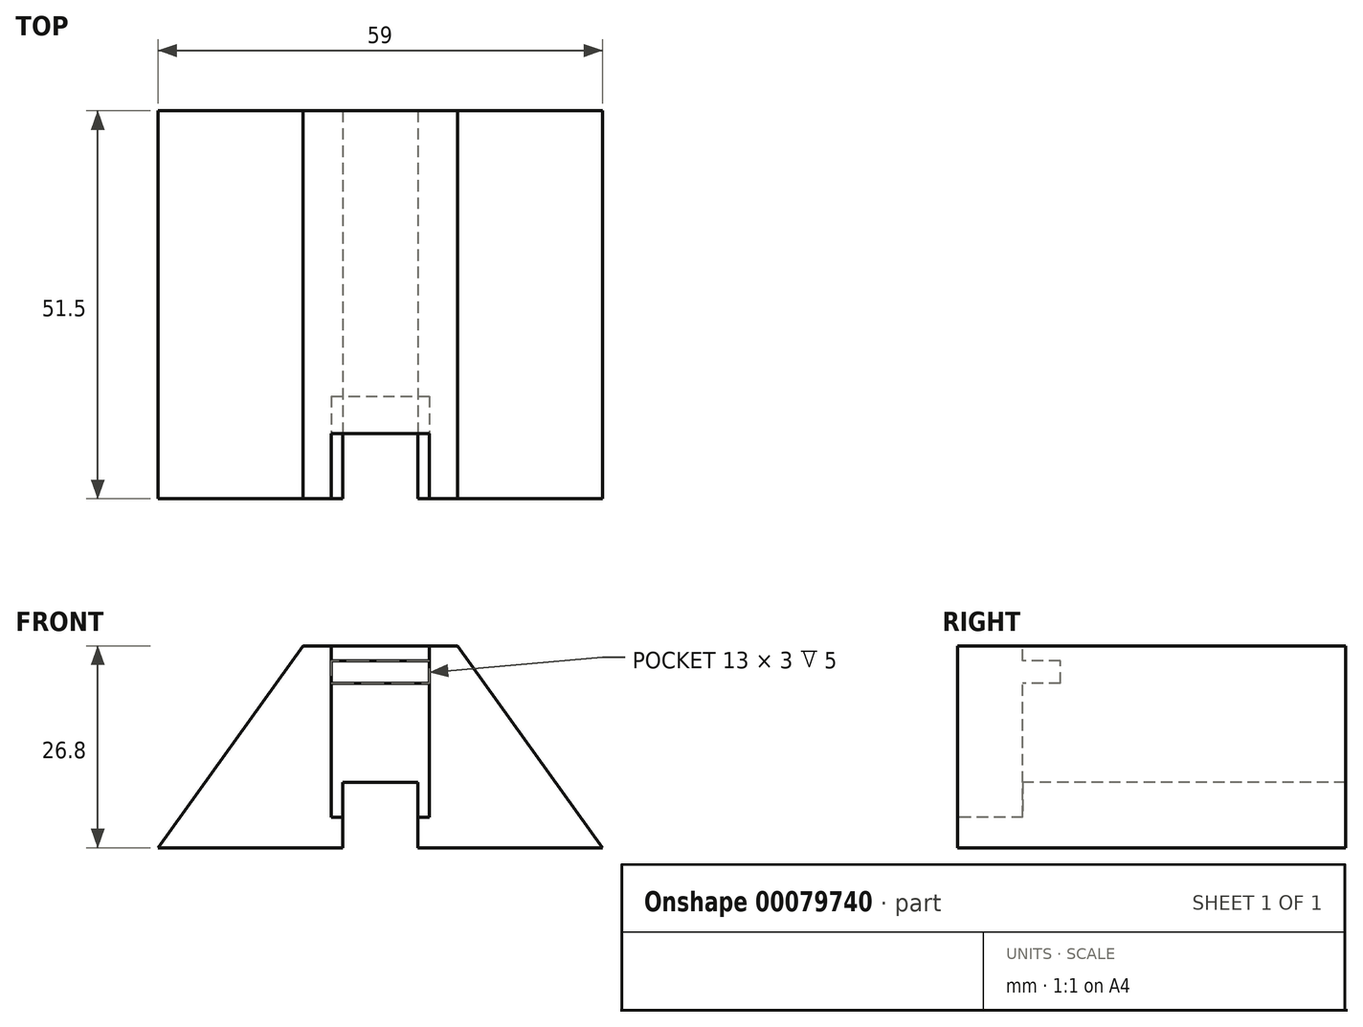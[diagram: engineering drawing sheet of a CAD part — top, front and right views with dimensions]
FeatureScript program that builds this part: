
annotation { "Feature Type Name" : "Feature", "Feature Type Description" : "" }
export const myFeature = defineFeature(function(context is Context, id is Id, definition is map)
    precondition{}
    {
        {
            var Q0;
            Q0=qCreatedBy(makeId("Top.planeOp"),FACE);
            var sketch = newSketch(context, id + "F0", { "sketchPlane" : qUnion([Q0])});
            skLineSegment(sketch, "E0.bottom", {"start": v(-29.5, 25.75) * mm, "end": v(29.5, 25.75) * mm});
            skLineSegment(sketch, "E0.top", {"start": v(-29.5, -25.75) * mm, "end": v(29.5, -25.75) * mm});
            skLineSegment(sketch, "E0.left", {"start": v(-29.5, 25.75) * mm, "end": v(-29.5, -25.75) * mm});
            skLineSegment(sketch, "E0.right", {"start": v(29.5, 25.75) * mm, "end": v(29.5, -25.75) * mm});
            skPoint(sketch, "E0.middle", {"position": v(0, 0) * mm});
            skSolve(sketch);
        }
        {
            var Q0;
            Q0=makeQuery(id+"F0.imprint","IMPRINT",FACE,{"disambiguationData":[TD([[makeQuery(id+"F0.imprint","IMPRINT",EDGE,{"derivedFrom":sQuery(id+"F0.wireOp",EDGE,"E0.bottom")}),-1.0]])]});
            extrude(context, id + "F1", {"entities" : qUnion([Q0]), "depth" : 26.8 * mm});
        }
        {
            var Q0;
            Q0=makeQuery(id+"F1.opExtrude","CAP_FACE",FACE,{"disambiguationData":[OSD([sQuery(id+"F0.wireOp",EDGE,"E0.bottom"),sQuery(id+"F0.wireOp",EDGE,"E0.top"),sQuery(id+"F0.wireOp",EDGE,"E0.left"),sQuery(id+"F0.wireOp",EDGE,"E0.right")])],"isStart":false});
            var sketch = newSketch(context, id + "F2", { "sketchPlane" : qUnion([Q0])});
            skLineSegment(sketch, "E1.bottom", {"start": v(-5, -17.1) * mm, "end": v(5, -17.1) * mm});
            skLineSegment(sketch, "E1.top", {"start": v(-5, -25.75) * mm, "end": v(5, -25.75) * mm});
            skLineSegment(sketch, "E1.left", {"start": v(-5, -17.1) * mm, "end": v(-5, -25.75) * mm});
            skLineSegment(sketch, "E1.right", {"start": v(5, -17.1) * mm, "end": v(5, -25.75) * mm});
            skPoint(sketch, "E1.middle", {"position": v(0, -21.43) * mm});
            skSolve(sketch);
        }
        {
            var Q0;
            Q0=makeQuery(id+"F2.imprint","IMPRINT",FACE,{"disambiguationData":[TD([[makeQuery(id+"F2.imprint","IMPRINT",EDGE,{"derivedFrom":sQuery(id+"F2.wireOp",EDGE,"E1.bottom")}),-1.0]])]});
            extrude(context, id + "F3", {"entities" : qUnion([Q0]), "operationType" : NewBodyOperationType.REMOVE, "oppositeDirection" : true, "depth" : 26.8 * mm});
        }
        {
            var Q0;
            Q0=makeQuery(id+"F1.opExtrude","CAP_FACE",FACE,{"disambiguationData":[OSD([sQuery(id+"F0.wireOp",EDGE,"E0.bottom"),sQuery(id+"F0.wireOp",EDGE,"E0.top"),sQuery(id+"F0.wireOp",EDGE,"E0.left"),sQuery(id+"F0.wireOp",EDGE,"E0.right")])],"isStart":false});
            var sketch = newSketch(context, id + "F4", { "sketchPlane" : qUnion([Q0])});
            skLineSegment(sketch, "E2.bottom", {"start": v(-6.5, -17.1) * mm, "end": v(6.5, -17.1) * mm});
            skLineSegment(sketch, "E2.top", {"start": v(-6.5, -25.75) * mm, "end": v(6.5, -25.75) * mm});
            skLineSegment(sketch, "E2.left", {"start": v(-6.5, -17.1) * mm, "end": v(-6.5, -25.75) * mm});
            skLineSegment(sketch, "E2.right", {"start": v(6.5, -17.1) * mm, "end": v(6.5, -25.75) * mm});
            skPoint(sketch, "E2.middle", {"position": v(0, -21.43) * mm});
            skSolve(sketch);
        }
        {
            var Q0;
            {var subQ3=sQuery(id+"F4.wireOp",EDGE,"E2.left");Q0=makeQuery(id+"F4.imprint","IMPRINT",FACE,{"disambiguationData":[TD([[makeQuery(id+"F4.imprint","IMPRINT",EDGE,{"derivedFrom":subQ3}),1.0]])]});}
            var Q1;
            {var subQ3=sQuery(id+"F4.wireOp",EDGE,"E2.right");Q1=makeQuery(id+"F4.imprint","IMPRINT",FACE,{"disambiguationData":[TD([[makeQuery(id+"F4.imprint","IMPRINT",EDGE,{"derivedFrom":subQ3}),-1.0]])]});}
            extrude(context, id + "F5", {"entities" : qUnion([Q0, Q1]), "operationType" : NewBodyOperationType.REMOVE, "oppositeDirection" : true, "depth" : 22.75 * mm});
        }
        {
            var Q0;
            {var subQ1=sQuery(id+"F0.wireOp",EDGE,"E0.left");var subQ2=sQuery(id+"F0.wireOp",EDGE,"E0.top");Q0=makeQuery(id+"F3.boolean.opBoolean","SPLIT",FACE,{"disambiguationData":[TD([makeQuery(id+"F1.opExtrude","SWEPT_FACE",FACE,{"disambiguationData":[OSD([subQ1])]})])],"derivedFrom":makeQuery(id+"F1.opExtrude","SWEPT_FACE",FACE,{"disambiguationData":[OSD([subQ2])]})});}
            var sketch = newSketch(context, id + "F6", { "sketchPlane" : qUnion([Q0])});
            skLineSegment(sketch, "E3", {"start": v(-29.5, 0) * mm, "end": v(-10.24, 26.8) * mm});
            skSolve(sketch);
        }
        {
            var Q0;
            {var subQ0=sQuery(id+"F6.wireOp",EDGE,"E3");Q0=makeQuery(id+"F6.imprint","IMPRINT",FACE,{"disambiguationData":[TD([[makeQuery(id+"F6.imprint","IMPRINT",EDGE,{"derivedFrom":subQ0}),1.0]])]});}
            extrude(context, id + "F7", {"entities" : qUnion([Q0]), "operationType" : NewBodyOperationType.REMOVE, "oppositeDirection" : true, "depth" : 51.5 * mm});
        }
        {
            var Q0;
            {var subQ0=sQuery(id+"F0.wireOp",EDGE,"E0.right");var subQ2=sQuery(id+"F0.wireOp",EDGE,"E0.top");Q0=makeQuery(id+"F3.boolean.opBoolean","SPLIT",FACE,{"disambiguationData":[TD([makeQuery(id+"F1.opExtrude","SWEPT_FACE",FACE,{"disambiguationData":[OSD([subQ0])]})])],"derivedFrom":makeQuery(id+"F1.opExtrude","SWEPT_FACE",FACE,{"disambiguationData":[OSD([subQ2])]})});}
            var sketch = newSketch(context, id + "F8", { "sketchPlane" : qUnion([Q0])});
            skLineSegment(sketch, "E4", {"start": v(29.5, 0) * mm, "end": v(10.24, 26.8) * mm});
            skSolve(sketch);
        }
        {
            var Q0;
            {var subQ0=sQuery(id+"F8.wireOp",EDGE,"E4");Q0=makeQuery(id+"F8.imprint","IMPRINT",FACE,{"disambiguationData":[TD([[makeQuery(id+"F8.imprint","IMPRINT",EDGE,{"derivedFrom":subQ0}),-1.0]])]});}
            extrude(context, id + "F9", {"entities" : qUnion([Q0]), "operationType" : NewBodyOperationType.REMOVE, "oppositeDirection" : true, "depth" : 51.5 * mm});
        }
        {
            var Q0;
            {var subQ0=sQuery(id+"F4.wireOp",EDGE,"E2.bottom");Q0=makeQuery(id+"F5.boolean.opBoolean","MERGE",FACE,{"derivedFrom":[makeQuery(id+"F3.boolean.opBoolean","COPY",FACE,{"derivedFrom":makeQuery(id+"F3.opExtrude","SWEPT_FACE",FACE,{"disambiguationData":[OSD([sQuery(id+"F2.wireOp",EDGE,"E1.bottom")])]})}),makeQuery(id+"F5.opExtrude","SWEPT_FACE",FACE,{"disambiguationData":[OSD([subQ0]),TDD([makeQuery(id+"F4.imprint","IMPRINT",EDGE,{"disambiguationData":[TD([[makeQuery(id+"F4.imprint","INTERSECT",VERTEX,{"derivedFrom":[makeQuery(id+"F3.boolean.opBoolean","COPY",EDGE,{"derivedFrom":makeQuery(id+"F3.opExtrude","CAP_EDGE",EDGE,{"disambiguationData":[OSD([sQuery(id+"F2.wireOp",EDGE,"E1.left")])],"isStart":true})}),subQ0]}),1.0]])],"derivedFrom":subQ0})])]}),makeQuery(id+"F5.opExtrude","SWEPT_FACE",FACE,{"disambiguationData":[OSD([subQ0]),TDD([makeQuery(id+"F4.imprint","IMPRINT",EDGE,{"disambiguationData":[TD([[makeQuery(id+"F4.imprint","INTERSECT",VERTEX,{"derivedFrom":[makeQuery(id+"F3.boolean.opBoolean","COPY",EDGE,{"derivedFrom":makeQuery(id+"F3.opExtrude","CAP_EDGE",EDGE,{"disambiguationData":[OSD([sQuery(id+"F2.wireOp",EDGE,"E1.right")])],"isStart":true})}),subQ0]}),-1.0]])],"derivedFrom":subQ0})])]})]});}
            var sketch = newSketch(context, id + "F10", { "sketchPlane" : qUnion([Q0])});
            skLineSegment(sketch, "E5.bottom", {"start": v(-5, 8.67) * mm, "end": v(5, 8.67) * mm});
            skLineSegment(sketch, "E5.top", {"start": v(-5, 0) * mm, "end": v(5, 0) * mm});
            skLineSegment(sketch, "E5.left", {"start": v(-5, 8.67) * mm, "end": v(-5, 0) * mm});
            skLineSegment(sketch, "E5.right", {"start": v(5, 8.67) * mm, "end": v(5, 0) * mm});
            skPoint(sketch, "E5.middle", {"position": v(0, 4.33) * mm});
            skSolve(sketch);
        }
        {
            var Q0;
            {var subQ4=sQuery(id+"F10.wireOp",EDGE,"E5.bottom");Q0=makeQuery(id+"F10.imprint","IMPRINT",FACE,{"disambiguationData":[TD([[makeQuery(id+"F10.imprint","IMPRINT",EDGE,{"derivedFrom":subQ4}),-1.0]])]});}
            extrude(context, id + "F11", {"entities" : qUnion([Q0]), "operationType" : NewBodyOperationType.REMOVE, "oppositeDirection" : true, "depth" : 51.5 * mm});
        }
        {
            var Q0;
            {var subQ0=sQuery(id+"F4.wireOp",EDGE,"E2.bottom");Q0=makeQuery(id+"F5.boolean.opBoolean","MERGE",FACE,{"derivedFrom":[makeQuery(id+"F3.boolean.opBoolean","COPY",FACE,{"derivedFrom":makeQuery(id+"F3.opExtrude","SWEPT_FACE",FACE,{"disambiguationData":[OSD([sQuery(id+"F2.wireOp",EDGE,"E1.bottom")])]})}),makeQuery(id+"F5.opExtrude","SWEPT_FACE",FACE,{"disambiguationData":[OSD([subQ0]),TDD([makeQuery(id+"F4.imprint","IMPRINT",EDGE,{"disambiguationData":[TD([[makeQuery(id+"F4.imprint","INTERSECT",VERTEX,{"derivedFrom":[makeQuery(id+"F3.boolean.opBoolean","COPY",EDGE,{"derivedFrom":makeQuery(id+"F3.opExtrude","CAP_EDGE",EDGE,{"disambiguationData":[OSD([sQuery(id+"F2.wireOp",EDGE,"E1.left")])],"isStart":true})}),subQ0]}),1.0]])],"derivedFrom":subQ0})])]}),makeQuery(id+"F5.opExtrude","SWEPT_FACE",FACE,{"disambiguationData":[OSD([subQ0]),TDD([makeQuery(id+"F4.imprint","IMPRINT",EDGE,{"disambiguationData":[TD([[makeQuery(id+"F4.imprint","INTERSECT",VERTEX,{"derivedFrom":[makeQuery(id+"F3.boolean.opBoolean","COPY",EDGE,{"derivedFrom":makeQuery(id+"F3.opExtrude","CAP_EDGE",EDGE,{"disambiguationData":[OSD([sQuery(id+"F2.wireOp",EDGE,"E1.right")])],"isStart":true})}),subQ0]}),-1.0]])],"derivedFrom":subQ0})])]})]});}
            var sketch = newSketch(context, id + "F12", { "sketchPlane" : qUnion([Q0])});
            skLineSegment(sketch, "E6.bottom", {"start": v(-6.5, 24.8) * mm, "end": v(6.5, 24.8) * mm});
            skLineSegment(sketch, "E6.top", {"start": v(-6.5, 21.8) * mm, "end": v(6.5, 21.8) * mm});
            skLineSegment(sketch, "E6.left", {"start": v(-6.5, 24.8) * mm, "end": v(-6.5, 21.8) * mm});
            skLineSegment(sketch, "E6.right", {"start": v(6.5, 24.8) * mm, "end": v(6.5, 21.8) * mm});
            skPoint(sketch, "E6.middle", {"position": v(0, 23.3) * mm});
            skSolve(sketch);
        }
        {
            var Q0;
            Q0=makeQuery(id+"F12.imprint","IMPRINT",FACE,{"disambiguationData":[TD([[makeQuery(id+"F12.imprint","IMPRINT",EDGE,{"derivedFrom":sQuery(id+"F12.wireOp",EDGE,"E6.bottom")}),-1.0]])]});
            extrude(context, id + "F13", {"entities" : qUnion([Q0]), "operationType" : NewBodyOperationType.REMOVE, "oppositeDirection" : true, "depth" : 5 * mm});
        }
    });
